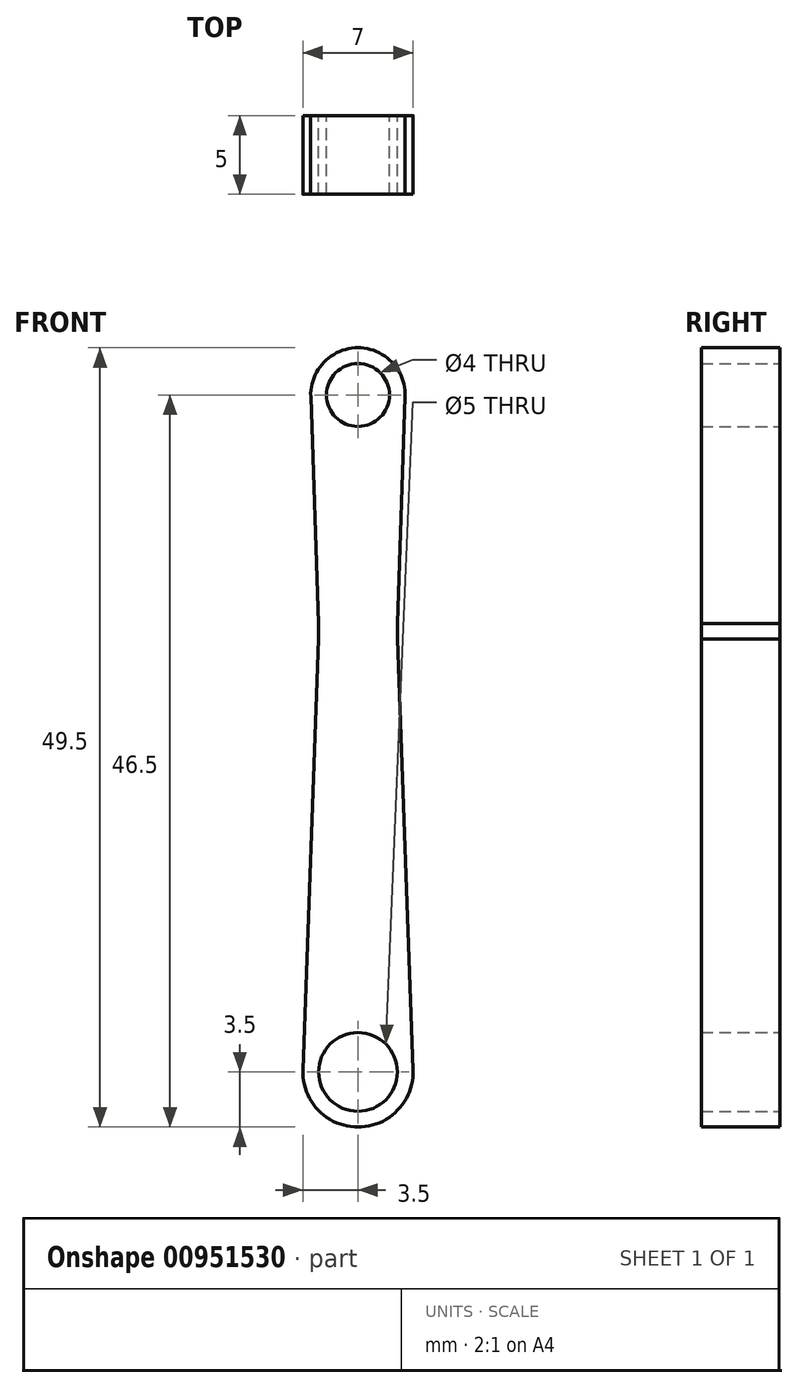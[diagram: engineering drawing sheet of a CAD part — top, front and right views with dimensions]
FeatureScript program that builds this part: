
annotation { "Feature Type Name" : "Feature", "Feature Type Description" : "" }
export const myFeature = defineFeature(function(context is Context, id is Id, definition is map)
    precondition{}
    {
        {
            var Q0;
            Q0=qCreatedBy(makeId("Front.planeOp"),FACE);
            var sketch = newSketch(context, id + "F0", { "sketchPlane" : qUnion([Q0])});
            skCircle(sketch, "E0", {"center": v(0, 0) * mm, "radius": 2 * mm});
            skCircle(sketch, "E1", {"center": v(0, -43) * mm, "radius": 2.5 * mm});
            skCircle(sketch, "E2", {"center": v(0, 0) * mm, "radius": 3 * mm});
            skCircle(sketch, "E3", {"center": v(0, -43) * mm, "radius": 3.5 * mm});
            skLineSegment(sketch, "E4.bottom", {"start": v(-2.5, -15.5) * mm, "end": v(2.5, -15.5) * mm});
            skLineSegment(sketch, "E4.top", {"start": v(-2.5, -14.5) * mm, "end": v(2.5, -14.5) * mm});
            skLineSegment(sketch, "E4.left", {"start": v(-2.5, -15.5) * mm, "end": v(-2.5, -14.5) * mm});
            skLineSegment(sketch, "E4.right", {"start": v(2.5, -15.5) * mm, "end": v(2.5, -14.5) * mm});
            skPoint(sketch, "E4.middle", {"position": v(0, -15) * mm});
            skLineSegment(sketch, "E5", {"start": v(3, -0.1) * mm, "end": v(2.5, -14.5) * mm});
            skLineSegment(sketch, "E6", {"start": v(-2.5, -14.5) * mm, "end": v(-3, -0.1) * mm});
            skLineSegment(sketch, "E7", {"start": v(-2.5, -15.5) * mm, "end": v(-3.5, -42.87) * mm});
            skLineSegment(sketch, "E8", {"start": v(2.5, -15.5) * mm, "end": v(3.5, -42.87) * mm});
            skSolve(sketch);
        }
        {
            var Q0;
            Q0 = qSketchRegion(id + "F0", true);
            extrude(context, id + "F1", {"entities" : qUnion([Q0]), "depth" : 5 * mm, "offsetDistance" : 25 * mm});
        }
    });
